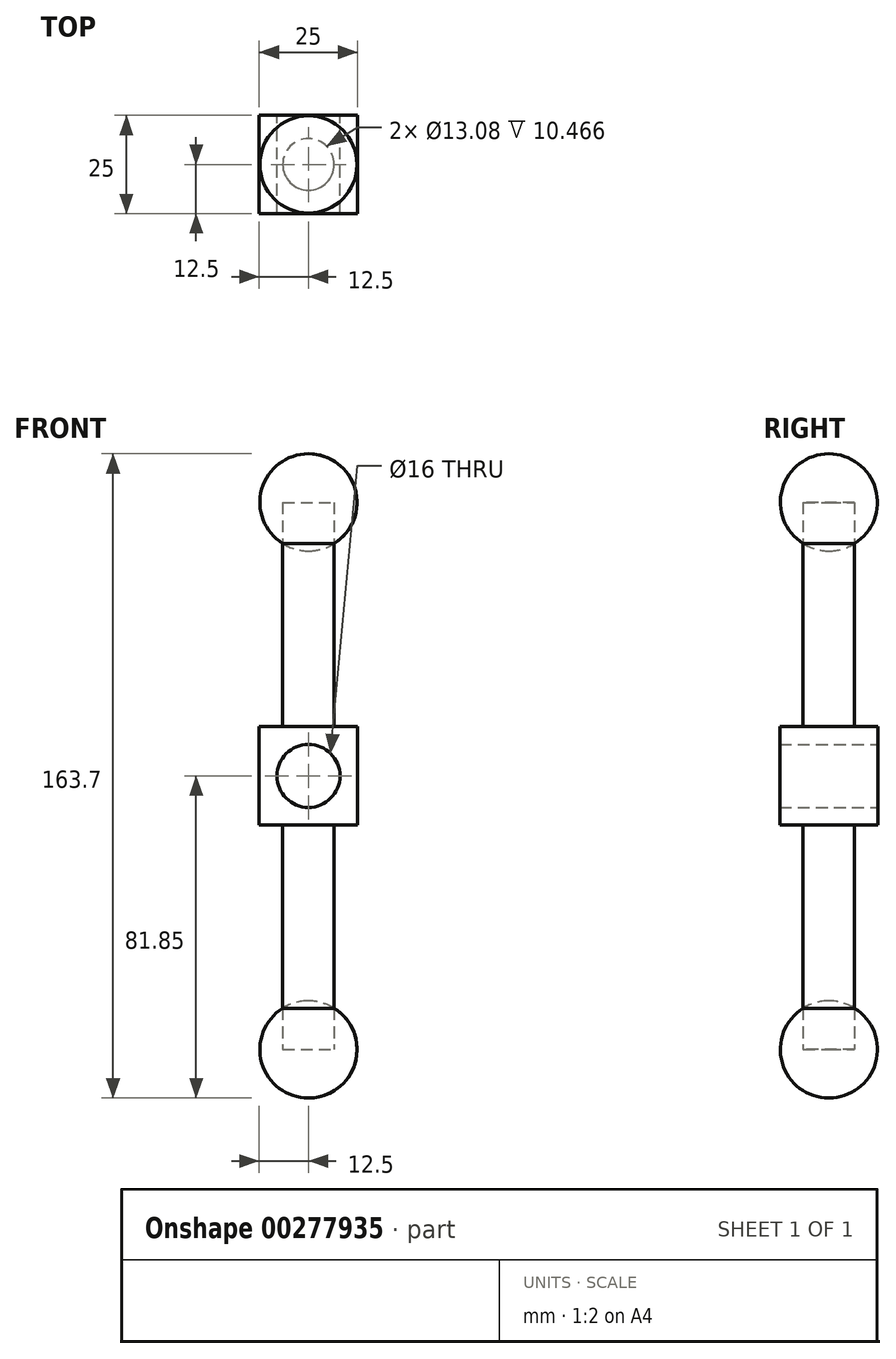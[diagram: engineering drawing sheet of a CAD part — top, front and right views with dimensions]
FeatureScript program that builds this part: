
annotation { "Feature Type Name" : "Feature", "Feature Type Description" : "" }
export const myFeature = defineFeature(function(context is Context, id is Id, definition is map)
    precondition{}
    {
        {
            var Q0;
            Q0=qCreatedBy(makeId("Front.planeOp"),FACE);
            var sketch = newSketch(context, id + "F0", { "sketchPlane" : qUnion([Q0])});
            skLineSegment(sketch, "E0.bottom", {"start": v(-6.54, -69.5) * mm, "end": v(6.54, -69.5) * mm});
            skLineSegment(sketch, "E0.top", {"start": v(-6.54, 69.5) * mm, "end": v(6.54, 69.5) * mm});
            skLineSegment(sketch, "E0.left", {"start": v(-6.54, -69.5) * mm, "end": v(-6.54, 69.5) * mm});
            skLineSegment(sketch, "E0.right", {"start": v(6.54, -69.5) * mm, "end": v(6.54, 69.5) * mm});
            skPoint(sketch, "E0.middle", {"position": v(0, 0) * mm});
            skCircle(sketch, "E1", {"center": v(0, 69.5) * mm, "radius": 12.34 * mm});
            skCircle(sketch, "E2", {"center": v(0, -69.5) * mm, "radius": 12.34 * mm});
            skLineSegment(sketch, "E3.bottom", {"start": v(12.5, -12.5) * mm, "end": v(-12.5, -12.5) * mm});
            skLineSegment(sketch, "E3.top", {"start": v(12.5, 12.5) * mm, "end": v(-12.5, 12.5) * mm});
            skLineSegment(sketch, "E3.left", {"start": v(12.5, -12.5) * mm, "end": v(12.5, 12.5) * mm});
            skLineSegment(sketch, "E3.right", {"start": v(-12.5, -12.5) * mm, "end": v(-12.5, 12.5) * mm});
            skCircle(sketch, "E4", {"center": v(0, 0) * mm, "radius": 8 * mm});
            skLineSegment(sketch, "E5", {"start": v(0, 69.5) * mm, "end": v(0, -69.5) * mm});
            skLineSegment(sketch, "E6", {"start": v(0, 69.5) * mm, "end": v(0, 81.85) * mm});
            skLineSegment(sketch, "E7", {"start": v(0, -69.5) * mm, "end": v(0, -81.85) * mm});
            skSolve(sketch);
        }
        {
            var Q0;
            {var subQ0=sQuery(id+"F0.wireOp",EDGE,"E3.right");Q0=makeQuery(id+"F0.imprint","IMPRINT",FACE,{"disambiguationData":[TD([[makeQuery(id+"F0.imprint","IMPRINT",EDGE,{"derivedFrom":subQ0}),-1.0]])]});}
            var Q1;
            {var subQ0=sQuery(id+"F0.wireOp",EDGE,"E3.left");Q1=makeQuery(id+"F0.imprint","IMPRINT",FACE,{"disambiguationData":[TD([[makeQuery(id+"F0.imprint","IMPRINT",EDGE,{"derivedFrom":subQ0}),1.0]])]});}
            var Q2;
            {var subQ0=sQuery(id+"F0.wireOp",EDGE,"E3.top");var subQ1=sQuery(id+"F0.wireOp",EDGE,"E0.left");var subQ2=makeQuery(id+"F0.imprint","INTERSECT",VERTEX,{"derivedFrom":[subQ1,subQ0]});Q2=makeQuery(id+"F0.imprint","IMPRINT",FACE,{"disambiguationData":[TD([[makeQuery(id+"F0.imprint","IMPRINT",EDGE,{"disambiguationData":[TD([[subQ2,1.0]])],"derivedFrom":subQ1}),-1.0]])]});}
            var Q3;
            {var subQ0=sQuery(id+"F0.wireOp",EDGE,"E3.bottom");var subQ1=sQuery(id+"F0.wireOp",EDGE,"E0.left");var subQ2=makeQuery(id+"F0.imprint","INTERSECT",VERTEX,{"derivedFrom":[subQ1,subQ0]});Q3=makeQuery(id+"F0.imprint","IMPRINT",FACE,{"disambiguationData":[TD([[makeQuery(id+"F0.imprint","IMPRINT",EDGE,{"disambiguationData":[TD([[subQ2,-1.0]])],"derivedFrom":subQ1}),-1.0]])]});}
            var Q4;
            {var subQ0=sQuery(id+"F0.wireOp",EDGE,"E3.top");var subQ1=sQuery(id+"F0.wireOp",EDGE,"E0.right");var subQ2=makeQuery(id+"F0.imprint","INTERSECT",VERTEX,{"derivedFrom":[subQ1,subQ0]});Q4=makeQuery(id+"F0.imprint","IMPRINT",FACE,{"disambiguationData":[TD([[makeQuery(id+"F0.imprint","IMPRINT",EDGE,{"disambiguationData":[TD([[subQ2,1.0]])],"derivedFrom":subQ1}),1.0]])]});}
            var Q5;
            {var subQ0=sQuery(id+"F0.wireOp",EDGE,"E3.bottom");var subQ1=sQuery(id+"F0.wireOp",EDGE,"E0.right");var subQ2=makeQuery(id+"F0.imprint","INTERSECT",VERTEX,{"derivedFrom":[subQ1,subQ0]});Q5=makeQuery(id+"F0.imprint","IMPRINT",FACE,{"disambiguationData":[TD([[makeQuery(id+"F0.imprint","IMPRINT",EDGE,{"disambiguationData":[TD([[subQ2,-1.0]])],"derivedFrom":subQ1}),1.0]])]});}
            extrude(context, id + "F1", {"entities" : qUnion([Q0, Q1, Q2, Q3, Q4, Q5]), "endBound" : BoundingType.SYMMETRIC, "depth" : 25 * mm});
        }
        {
            var Q0;
            {var subQ0=sQuery(id+"F0.wireOp",EDGE,"E3.top");var subQ1=sQuery(id+"F0.wireOp",EDGE,"E0.right");var subQ2=makeQuery(id+"F0.imprint","INTERSECT",VERTEX,{"derivedFrom":[subQ1,subQ0]});Q0=makeQuery(id+"F0.imprint","IMPRINT",FACE,{"disambiguationData":[TD([[makeQuery(id+"F0.imprint","IMPRINT",EDGE,{"disambiguationData":[TD([[subQ2,-1.0]])],"derivedFrom":subQ1}),1.0]])]});}
            var Q1;
            {var subQ0=sQuery(id+"F0.wireOp",EDGE,"E2");var subQ1=sQuery(id+"F0.wireOp",EDGE,"E0.right");var subQ2=makeQuery(id+"F0.imprint","INTERSECT",VERTEX,{"derivedFrom":[subQ1,subQ0]});Q1=makeQuery(id+"F0.imprint","IMPRINT",FACE,{"disambiguationData":[TD([[makeQuery(id+"F0.imprint","IMPRINT",EDGE,{"disambiguationData":[TD([[subQ2,-1.0]])],"derivedFrom":subQ1}),1.0]])]});}
            var Q2;
            Q2=sQuery(id+"F0.wireOp",EDGE,"E5");
            revolve(context, id + "F2", {"entities" : qUnion([Q0, Q1]), "axis" : qUnion([Q2]), "revolveType" : RevolveType.FULL});
        }
        {
            var Q0;
            {var subQ3=sQuery(id+"F0.wireOp",EDGE,"E6");Q0=makeQuery(id+"F0.imprint","IMPRINT",FACE,{"disambiguationData":[TD([[makeQuery(id+"F0.imprint","IMPRINT",EDGE,{"derivedFrom":subQ3}),-1.0]])]});}
            var Q1;
            {var subQ3=sQuery(id+"F0.wireOp",EDGE,"E7");Q1=makeQuery(id+"F0.imprint","IMPRINT",FACE,{"disambiguationData":[TD([[makeQuery(id+"F0.imprint","IMPRINT",EDGE,{"derivedFrom":subQ3}),1.0]])]});}
            var Q2;
            Q2=sQuery(id+"F0.wireOp",EDGE,"E6");
            revolve(context, id + "F3", {"entities" : qUnion([Q0, Q1]), "axis" : qUnion([Q2]), "revolveType" : RevolveType.FULL});
        }
        {
            var Q0;
            Q0=makeQuery(id+"F1.opExtrude","SWEPT_BODY",BODY,{"disambiguationData":[OSD([sQuery(id+"F0.wireOp",EDGE,"E3.bottom"),sQuery(id+"F0.wireOp",EDGE,"E3.top"),sQuery(id+"F0.wireOp",EDGE,"E3.left"),sQuery(id+"F0.wireOp",EDGE,"E3.right"),sQuery(id+"F0.wireOp",EDGE,"E4")])]});
            var Q1;
            Q1=makeQuery(id+"F2.opRevolve","SWEPT_BODY",BODY,{"disambiguationData":[OSD([sQuery(id+"F0.wireOp",EDGE,"E0.right"),sQuery(id+"F0.wireOp",EDGE,"E1"),sQuery(id+"F0.wireOp",EDGE,"E3.top"),sQuery(id+"F0.wireOp",EDGE,"E5")])]});
            var Q2;
            Q2=makeQuery(id+"F2.opRevolve","SWEPT_BODY",BODY,{"disambiguationData":[OSD([sQuery(id+"F0.wireOp",EDGE,"E0.right"),sQuery(id+"F0.wireOp",EDGE,"E2"),sQuery(id+"F0.wireOp",EDGE,"E3.bottom"),sQuery(id+"F0.wireOp",EDGE,"E5")])]});
            var Q3;
            Q3=makeQuery(id+"F3.opRevolve","SWEPT_BODY",BODY,{"disambiguationData":[OSD([sQuery(id+"F0.wireOp",EDGE,"E0.top"),sQuery(id+"F0.wireOp",EDGE,"E0.right"),sQuery(id+"F0.wireOp",EDGE,"E1"),sQuery(id+"F0.wireOp",EDGE,"E6")])]});
            var Q4;
            Q4=makeQuery(id+"F3.opRevolve","SWEPT_BODY",BODY,{"disambiguationData":[OSD([sQuery(id+"F0.wireOp",EDGE,"E0.bottom"),sQuery(id+"F0.wireOp",EDGE,"E0.right"),sQuery(id+"F0.wireOp",EDGE,"E2"),sQuery(id+"F0.wireOp",EDGE,"E7")])]});
            booleanBodies(context, id + "F4", {"operationType" : BooleanOperationType.UNION, "tools" : qUnion([Q0, Q1, Q2, Q3, Q4])});
        }
    });
